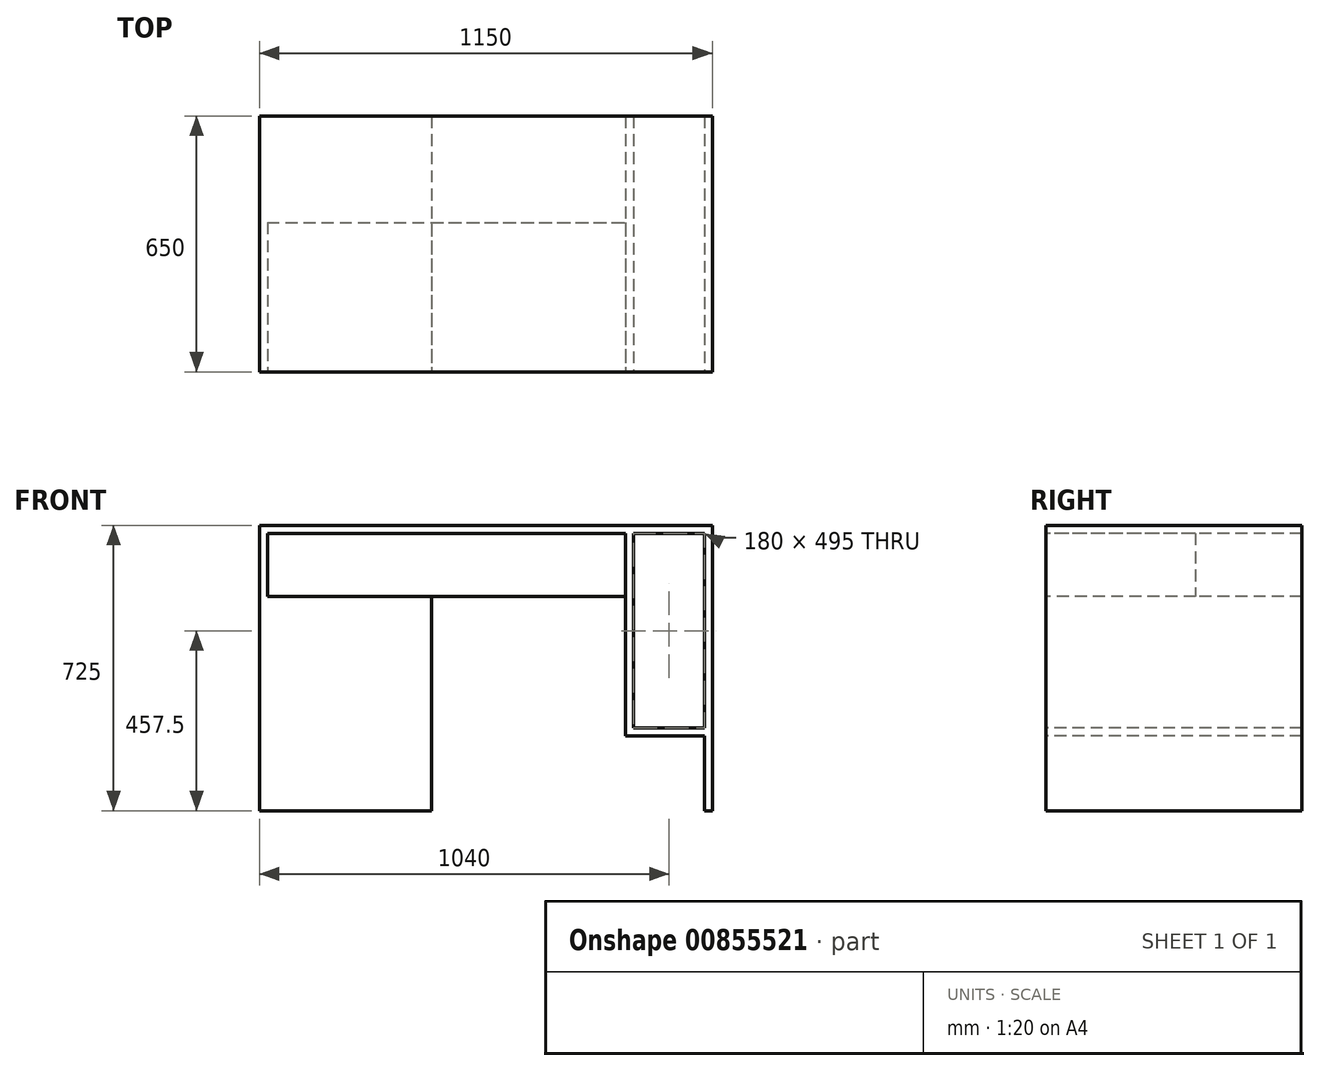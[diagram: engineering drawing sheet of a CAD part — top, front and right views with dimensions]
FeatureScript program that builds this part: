
annotation { "Feature Type Name" : "Feature", "Feature Type Description" : "" }
export const myFeature = defineFeature(function(context is Context, id is Id, definition is map)
    precondition{}
    {
        {
            var Q0;
            Q0=qCreatedBy(makeId("Top.planeOp"),FACE);
            var sketch = newSketch(context, id + "F0", { "sketchPlane" : qUnion([Q0])});
            skLineSegment(sketch, "E0.bottom", {"start": v(-1150, 310.4) * mm, "end": v(0, 310.4) * mm});
            skLineSegment(sketch, "E0.top", {"start": v(-1150, -339.6) * mm, "end": v(0, -339.6) * mm});
            skLineSegment(sketch, "E0.left", {"start": v(-1150, 310.4) * mm, "end": v(-1150, -339.6) * mm});
            skLineSegment(sketch, "E0.right", {"start": v(0, 310.4) * mm, "end": v(0, -339.6) * mm});
            skSolve(sketch);
        }
        {
            var Q0;
            Q0=makeQuery(id+"F0.imprint","IMPRINT",FACE,{"disambiguationData":[TD([[makeQuery(id+"F0.imprint","IMPRINT",EDGE,{"derivedFrom":sQuery(id+"F0.wireOp",EDGE,"E0.bottom")}),-1.0]])]});
            extrude(context, id + "F1", {"entities" : qUnion([Q0]), "depth" : 725 * mm, "offsetDistance" : 25.4 * mm});
        }
        {
            var Q0;
            Q0=makeQuery(id+"F1.opExtrude","SWEPT_FACE",FACE,{"disambiguationData":[OSD([sQuery(id+"F0.wireOp",EDGE,"E0.top")])]});
            var sketch = newSketch(context, id + "F2", { "sketchPlane" : qUnion([Q0])});
            skLineSegment(sketch, "E1.bottom", {"start": v(-200, 705) * mm, "end": v(-20, 705) * mm});
            skLineSegment(sketch, "E1.top", {"start": v(-200, 210) * mm, "end": v(-20, 210) * mm});
            skLineSegment(sketch, "E1.left", {"start": v(-200, 705) * mm, "end": v(-200, 210) * mm});
            skLineSegment(sketch, "E1.right", {"start": v(-20, 705) * mm, "end": v(-20, 210) * mm});
            skSolve(sketch);
        }
        {
            var Q0;
            Q0=makeQuery(id+"F2.imprint","IMPRINT",FACE,{"disambiguationData":[TD([[makeQuery(id+"F2.imprint","IMPRINT",EDGE,{"derivedFrom":sQuery(id+"F2.wireOp",EDGE,"E1.bottom")}),-1.0]])]});
            extrude(context, id + "F3", {"entities" : qUnion([Q0]), "operationType" : NewBodyOperationType.REMOVE, "endBound" : BoundingType.THROUGH_ALL, "oppositeDirection" : true, "depth" : 25.4 * mm, "offsetDistance" : 25.4 * mm});
        }
        {
            var Q0;
            Q0=makeQuery(id+"F1.opExtrude","SWEPT_FACE",FACE,{"disambiguationData":[OSD([sQuery(id+"F0.wireOp",EDGE,"E0.top")])]});
            var sketch = newSketch(context, id + "F4", { "sketchPlane" : qUnion([Q0])});
            skLineSegment(sketch, "E2.bottom", {"start": v(-712.68, 545) * mm, "end": v(-220, 545) * mm});
            skLineSegment(sketch, "E2.top", {"start": v(-712.68, 0) * mm, "end": v(-220, 0) * mm});
            skLineSegment(sketch, "E2.left", {"start": v(-712.68, 545) * mm, "end": v(-712.68, 0) * mm});
            skLineSegment(sketch, "E3.bottom", {"start": v(-220, 190) * mm, "end": v(-20, 190) * mm});
            skLineSegment(sketch, "E3.top", {"start": v(-220, 0) * mm, "end": v(-20, 0) * mm});
            skLineSegment(sketch, "E3.right", {"start": v(-20, 190) * mm, "end": v(-20, 0) * mm});
            skLineSegment(sketch, "E4", {"start": v(-220, 545) * mm, "end": v(-220, 190) * mm});
            skSolve(sketch);
        }
        {
            var Q0;
            Q0=makeQuery(id+"F4.imprint","IMPRINT",FACE,{"disambiguationData":[TD([[makeQuery(id+"F4.imprint","IMPRINT",EDGE,{"derivedFrom":sQuery(id+"F4.wireOp",EDGE,"E2.bottom")}),-1.0]])]});
            extrude(context, id + "F5", {"entities" : qUnion([Q0]), "operationType" : NewBodyOperationType.REMOVE, "endBound" : BoundingType.THROUGH_ALL, "oppositeDirection" : true, "depth" : 25.4 * mm, "offsetDistance" : 25.4 * mm});
        }
        {
            var Q0;
            Q0=makeQuery(id+"F1.opExtrude","SWEPT_FACE",FACE,{"disambiguationData":[OSD([sQuery(id+"F0.wireOp",EDGE,"E0.top")])]});
            var sketch = newSketch(context, id + "F6", { "sketchPlane" : qUnion([Q0])});
            skLineSegment(sketch, "E5.bottom", {"start": v(-1130, 705) * mm, "end": v(-220, 705) * mm});
            skLineSegment(sketch, "E5.top", {"start": v(-1130, 545) * mm, "end": v(-220, 545) * mm});
            skLineSegment(sketch, "E5.left", {"start": v(-1130, 705) * mm, "end": v(-1130, 545) * mm});
            skLineSegment(sketch, "E5.right", {"start": v(-220, 705) * mm, "end": v(-220, 545) * mm});
            skSolve(sketch);
        }
        {
            var Q0;
            Q0=makeQuery(id+"F6.imprint","IMPRINT",FACE,{"disambiguationData":[TD([[makeQuery(id+"F6.imprint","IMPRINT",EDGE,{"derivedFrom":sQuery(id+"F6.wireOp",EDGE,"E5.bottom")}),-1.0]])]});
            extrude(context, id + "F7", {"entities" : qUnion([Q0]), "operationType" : NewBodyOperationType.REMOVE, "oppositeDirection" : true, "depth" : 380 * mm, "offsetDistance" : 25.4 * mm});
        }
    });
